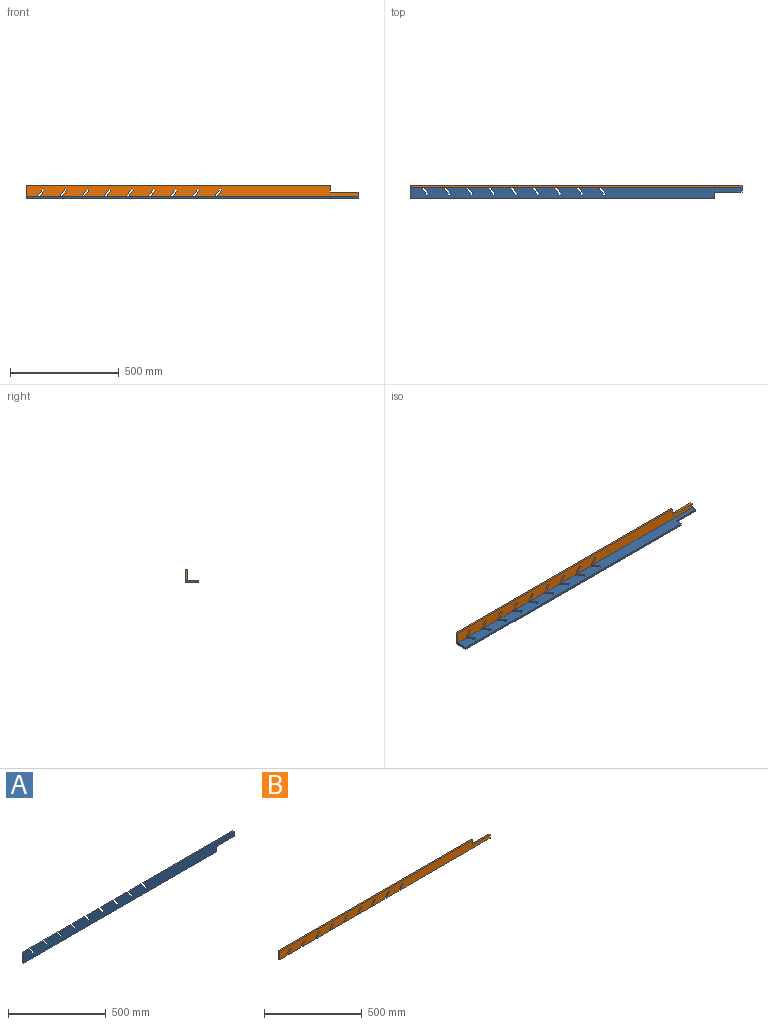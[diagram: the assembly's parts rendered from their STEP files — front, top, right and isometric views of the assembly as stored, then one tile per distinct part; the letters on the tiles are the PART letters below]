
ASSEMBLY  parts=2 mates=1
PART A: 44 faces, bbox 1524x9.5x63.5 mm
  f0: plane 45.63x32.26mm, normal (0.82,0,0.58), area 532.3mm2, adj f1,f41,f42,f43
  f1: plane 9.53x8.3mm, normal (-0.58,0,0.82), area 96.8mm2, adj f0,f2,f42,f43
  f2: plane 39.76x28.12mm, normal (-0.82,0,-0.58), area 463.8mm2, adj f1,f3,f42,f43
  f3: plane 89.16x9.53mm, normal (0,0,1), area 849.2mm2, adj f2,f4,f42,f43
  f4: plane 45.63x32.26mm, normal (0.82,0,0.58), area 532.3mm2, adj f3,f5,f42,f43
  f5: plane 9.53x8.3mm, normal (-0.58,0,0.82), area 96.8mm2, adj f4,f6,f42,f43
  f6: plane 39.76x28.12mm, normal (-0.82,0,-0.58), area 463.8mm2, adj f5,f7,f42,f43
  f7: plane 654.18x9.53mm, normal (0,0,1), area 6231mm2, adj f6,f8,f42,f43
  f8: plane 31.75x9.53mm, normal (1,0,0), area 302.4mm2, adj f7,f9,f42,f43
  f9: plane 127x9.53mm, normal (0,0,-1), area 1209.7mm2, adj f8,f10,f42,f43
  f10: plane 31.75x9.53mm, normal (1,0,0), area 302.4mm2, adj f9,f11,f42,f43
  f11: plane 1397x9.53mm, normal (0,0,-1), area 13306.4mm2, adj f10,f12,f42,f43
  f12: plane 63.5x9.53mm, normal (-1,0,0), area 604.8mm2, adj f11,f13,f42,f43
  f13: plane 44.58x9.53mm, normal (0,0,1), area 424.6mm2, adj f12,f14,f42,f43
  f14: plane 45.63x32.26mm, normal (0.82,0,0.58), area 532.3mm2, adj f13,f15,f42,f43
  f15: plane 9.53x8.3mm, normal (-0.58,0,0.82), area 96.8mm2, adj f14,f16,f42,f43
  f16: plane 39.76x28.12mm, normal (-0.82,0,-0.58), area 463.8mm2, adj f15,f17,f42,f43
  f17: plane 89.16x9.53mm, normal (0,0,1), area 849.2mm2, adj f16,f18,f42,f43
  f18: plane 45.63x32.26mm, normal (0.82,0,0.58), area 532.3mm2, adj f17,f19,f42,f43
  f19: plane 9.53x8.3mm, normal (-0.58,0,0.82), area 96.8mm2, adj f18,f20,f42,f43
  f20: plane 39.76x28.12mm, normal (-0.82,0,-0.58), area 463.8mm2, adj f19,f21,f42,f43
  f21: plane 89.16x9.53mm, normal (0,0,1), area 849.2mm2, adj f20,f22,f42,f43
  f22: plane 45.63x32.26mm, normal (0.82,0,0.58), area 532.3mm2, adj f21,f23,f42,f43
  f23: plane 9.53x8.3mm, normal (-0.58,0,0.82), area 96.8mm2, adj f22,f24,f42,f43
  f24: plane 39.76x28.12mm, normal (-0.82,0,-0.58), area 463.8mm2, adj f23,f25,f42,f43
  f25: plane 89.16x9.53mm, normal (0,0,1), area 849.2mm2, adj f24,f26,f42,f43
  f26: plane 45.63x32.26mm, normal (0.82,0,0.58), area 532.3mm2, adj f25,f27,f42,f43
  f27: plane 9.53x8.3mm, normal (-0.58,0,0.82), area 96.8mm2, adj f26,f28,f42,f43
  f28: plane 39.76x28.12mm, normal (-0.82,0,-0.58), area 463.8mm2, adj f27,f29,f42,f43
  f29: plane 89.16x9.53mm, normal (0,0,1), area 849.2mm2, adj f28,f30,f42,f43
  f30: plane 45.63x32.26mm, normal (0.82,0,0.58), area 532.3mm2, adj f29,f31,f42,f43
  f31: plane 9.53x8.3mm, normal (-0.58,0,0.82), area 96.8mm2, adj f30,f32,f42,f43
  f32: plane 39.76x28.12mm, normal (-0.82,0,-0.58), area 463.8mm2, adj f31,f33,f42,f43
  f33: plane 89.16x9.53mm, normal (0,0,1), area 849.2mm2, adj f32,f34,f42,f43
  f34: plane 45.63x32.26mm, normal (0.82,0,0.58), area 532.3mm2, adj f33,f35,f42,f43
  f35: plane 9.53x8.3mm, normal (-0.58,0,0.82), area 96.8mm2, adj f34,f36,f42,f43
  f36: plane 39.76x28.12mm, normal (-0.82,0,-0.58), area 463.8mm2, adj f35,f37,f42,f43
  f37: plane 89.16x9.53mm, normal (0,0,1), area 849.2mm2, adj f36,f38,f42,f43
  f38: plane 45.63x32.26mm, normal (0.82,0,0.58), area 532.3mm2, adj f37,f39,f42,f43
  f39: plane 9.53x8.3mm, normal (-0.58,0,0.82), area 96.8mm2, adj f38,f40,f42,f43
  f40: plane 39.76x28.12mm, normal (-0.82,0,-0.58), area 463.8mm2, adj f39,f41,f42,f43
  f41: plane 89.16x9.53mm, normal (0,0,1), area 849.2mm2, adj f0,f40,f42,f43
  f42: plane 1524x63.5mm, normal (0,1,0), area 87960.4mm2, adj f0,f1,f2,f3,f4,f5,f6,f7
  f43: plane 1524x63.5mm, normal (0,-1,0), area 87960.4mm2, adj f0,f1,f2,f3,f4,f5,f6,f7
PART B: 44 faces, bbox 1524x9.5x54 mm
  f0: plane 89.16x9.53mm, normal (0,0,-1), area 849.2mm2, adj f1,f41,f42,f43
  f1: plane 30.24x21.38mm, normal (-0.82,0,0.58), area 352.7mm2, adj f0,f2,f42,f43
  f2: plane 9.53x8.3mm, normal (-0.58,0,-0.82), area 96.8mm2, adj f1,f3,f42,f43
  f3: plane 36.1x25.53mm, normal (0.82,0,-0.58), area 421.2mm2, adj f2,f4,f42,f43
  f4: plane 89.16x9.53mm, normal (0,0,-1), area 849.2mm2, adj f3,f5,f42,f43
  f5: plane 30.24x21.38mm, normal (-0.82,0,0.58), area 352.7mm2, adj f4,f6,f42,f43
  f6: plane 9.53x8.3mm, normal (-0.58,0,-0.82), area 96.8mm2, adj f5,f7,f42,f43
  f7: plane 36.1x25.53mm, normal (0.82,0,-0.58), area 421.2mm2, adj f6,f8,f42,f43
  f8: plane 89.16x9.53mm, normal (0,0,-1), area 849.2mm2, adj f7,f9,f42,f43
  f9: plane 30.24x21.38mm, normal (-0.82,0,0.58), area 352.7mm2, adj f8,f10,f42,f43
  f10: plane 9.53x8.3mm, normal (-0.58,0,-0.82), area 96.8mm2, adj f9,f11,f42,f43
  f11: plane 36.1x25.53mm, normal (0.82,0,-0.58), area 421.2mm2, adj f10,f12,f42,f43
  f12: plane 89.16x9.53mm, normal (0,0,-1), area 849.2mm2, adj f11,f13,f42,f43
  f13: plane 30.24x21.38mm, normal (-0.82,0,0.58), area 352.7mm2, adj f12,f14,f42,f43
  f14: plane 9.53x8.3mm, normal (-0.58,0,-0.82), area 96.8mm2, adj f13,f15,f42,f43
  f15: plane 36.1x25.53mm, normal (0.82,0,-0.58), area 421.2mm2, adj f14,f16,f42,f43
  f16: plane 89.16x9.53mm, normal (0,0,-1), area 849.2mm2, adj f15,f17,f42,f43
  f17: plane 30.24x21.38mm, normal (-0.82,0,0.58), area 352.7mm2, adj f16,f18,f42,f43
  f18: plane 9.53x8.3mm, normal (-0.58,0,-0.82), area 96.8mm2, adj f17,f19,f42,f43
  f19: plane 36.1x25.53mm, normal (0.82,0,-0.58), area 421.2mm2, adj f18,f20,f42,f43
  f20: plane 89.16x9.53mm, normal (0,0,-1), area 849.2mm2, adj f19,f21,f42,f43
  f21: plane 30.24x21.38mm, normal (-0.82,0,0.58), area 352.7mm2, adj f20,f22,f42,f43
  f22: plane 9.53x8.3mm, normal (-0.58,0,-0.82), area 96.8mm2, adj f21,f23,f42,f43
  f23: plane 36.1x25.53mm, normal (0.82,0,-0.58), area 421.2mm2, adj f22,f24,f42,f43
  f24: plane 51.31x9.53mm, normal (0,0,-1), area 488.8mm2, adj f23,f25,f42,f43
  f25: plane 53.98x9.53mm, normal (-1,0,0), area 514.1mm2, adj f24,f26,f42,f43
  f26: plane 1397x9.53mm, normal (0,0,1), area 13306.4mm2, adj f25,f27,f42,f43
  f27: plane 31.75x9.53mm, normal (1,0,0), area 302.4mm2, adj f26,f28,f42,f43
  f28: plane 127x9.53mm, normal (0,0,1), area 1209.7mm2, adj f27,f29,f42,f43
  f29: plane 22.23x9.53mm, normal (1,0,0), area 211.7mm2, adj f28,f30,f42,f43
  f30: plane 647.44x9.53mm, normal (0,0,-1), area 6166.9mm2, adj f29,f31,f42,f43
  f31: plane 30.24x21.38mm, normal (-0.82,0,0.58), area 352.7mm2, adj f30,f32,f42,f43
  f32: plane 9.53x8.3mm, normal (-0.58,0,-0.82), area 96.8mm2, adj f31,f33,f42,f43
  f33: plane 36.1x25.53mm, normal (0.82,0,-0.58), area 421.2mm2, adj f32,f34,f42,f43
  f34: plane 89.16x9.53mm, normal (0,0,-1), area 849.2mm2, adj f33,f35,f42,f43
  f35: plane 30.24x21.38mm, normal (-0.82,0,0.58), area 352.7mm2, adj f34,f36,f42,f43
  f36: plane 9.53x8.3mm, normal (-0.58,0,-0.82), area 96.8mm2, adj f35,f37,f42,f43
  f37: plane 36.1x25.53mm, normal (0.82,0,-0.58), area 421.2mm2, adj f36,f38,f42,f43
  f38: plane 89.16x9.53mm, normal (0,0,-1), area 849.2mm2, adj f37,f39,f42,f43
  f39: plane 30.24x21.38mm, normal (-0.82,0,0.58), area 352.7mm2, adj f38,f40,f42,f43
  f40: plane 9.53x8.3mm, normal (-0.58,0,-0.82), area 96.8mm2, adj f39,f41,f42,f43
  f41: plane 36.1x25.53mm, normal (0.82,0,-0.58), area 421.2mm2, adj f0,f40,f42,f43
  f42: plane 1524x53.98mm, normal (0,1,0), area 74511mm2, adj f0,f1,f2,f3,f4,f5,f6,f7
  f43: plane 1524x53.98mm, normal (0,-1,0), area 74511mm2, adj f0,f1,f2,f3,f4,f5,f6,f7
PLACE A rot(axis=(-1,0,0),90deg) t=(0,-31.75,-36.51)mm
PLACE B at identity
MATE parallel A.f43 <-> B.f24  axis (0,0,1) through (-762,0,-26.99)mm
